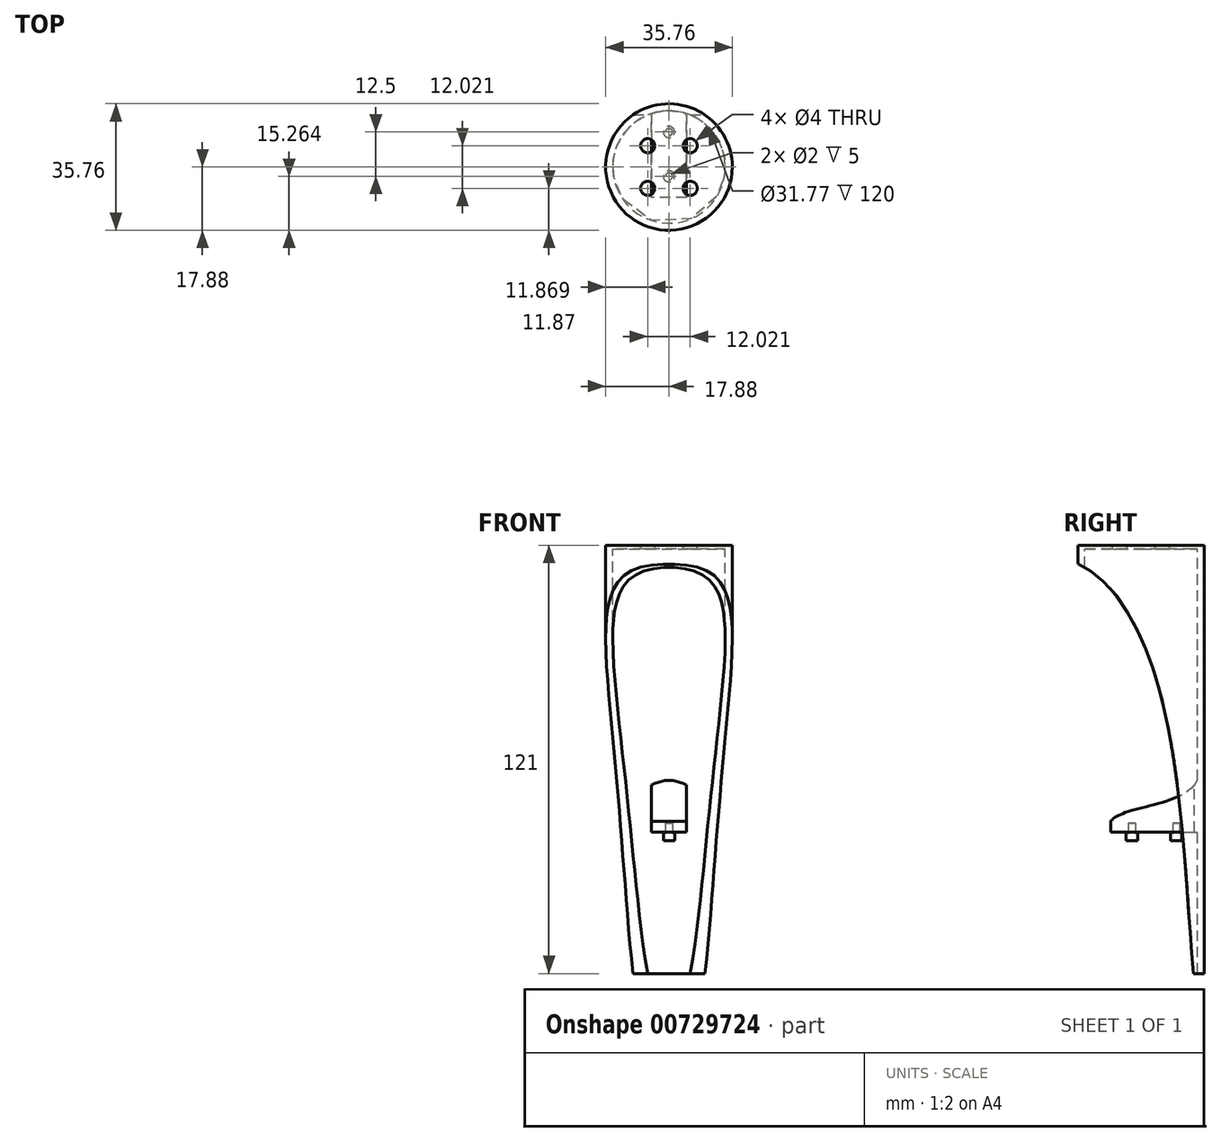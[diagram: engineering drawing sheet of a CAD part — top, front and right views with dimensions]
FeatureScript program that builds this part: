
annotation { "Feature Type Name" : "Feature", "Feature Type Description" : "" }
export const myFeature = defineFeature(function(context is Context, id is Id, definition is map)
    precondition{}
    {
        {
            var Q0;
            Q0=qCreatedBy(makeId("Top.planeOp"),FACE);
            var sketch = newSketch(context, id + "F0", { "sketchPlane" : qUnion([Q0])});
            skCircle(sketch, "E0", {"center": v(0, 0) * mm, "radius": 17.88 * mm});
            skSolve(sketch);
        }
        {
            var Q0;
            Q0=makeQuery(id+"F0.imprint","IMPRINT",FACE,{"disambiguationData":[TD([[makeQuery(id+"F0.imprint","IMPRINT",EDGE,{"derivedFrom":sQuery(id+"F0.wireOp",EDGE,"E0")}),1.0]])]});
            extrude(context, id + "F1", {"entities" : qUnion([Q0]), "depth" : 1 * mm, "offsetDistance" : 25 * mm});
        }
        {
            var Q0;
            Q0=makeQuery(id+"F1.opExtrude","CAP_FACE",FACE,{"disambiguationData":[OSD([sQuery(id+"F0.wireOp",EDGE,"E0")])],"isStart":true});
            var sketch = newSketch(context, id + "F2", { "sketchPlane" : qUnion([Q0])});
            skCircle(sketch, "E1", {"center": v(0, 0) * mm, "radius": 17.88 * mm});
            skCircle(sketch, "E2", {"center": v(0, 0) * mm, "radius": 15.88 * mm});
            skSolve(sketch);
        }
        {
            var Q0;
            Q0=qSketchRegion(id+"F2",true);
            extrude(context, id + "F3", {"entities" : qUnion([Q0]), "operationType" : NewBodyOperationType.ADD, "depth" : 120 * mm, "offsetDistance" : 25 * mm});
        }
        {
            var Q0;
            Q0=qCreatedBy(makeId("Right.planeOp"),FACE);
            var sketch = newSketch(context, id + "F4", { "sketchPlane" : qUnion([Q0])});
            skFitSpline(sketch, "E3", {"points": [v(-23.55, -2.93) * mm, v(2.93, -32.7) * mm, v(15.18, -125.34) * mm], "startDerivative": vector(85.56, -4.52) * mm, "endDerivative": vector(13.72, -154.47) * mm});
            skLineSegment(sketch, "E4", {"start": v(-23.55, -2.93) * mm, "end": v(-23.55, -130.52) * mm});
            skLineSegment(sketch, "E5", {"start": v(-23.55, -130.52) * mm, "end": v(15.18, -125.34) * mm});
            skSolve(sketch);
        }
        {
            var Q0;
            Q0=makeQuery(id+"F4.imprint","IMPRINT",FACE,{"disambiguationData":[TD([[makeQuery(id+"F4.imprint","IMPRINT",EDGE,{"derivedFrom":sQuery(id+"F4.wireOp",EDGE,"E3")}),-1.0]])]});
            extrude(context, id + "F5", {"entities" : qUnion([Q0]), "operationType" : NewBodyOperationType.REMOVE, "endBound" : BoundingType.SYMMETRIC, "oppositeDirection" : true, "depth" : 200 * mm, "offsetDistance" : 25 * mm});
        }
        {
            var Q0;
            Q0=makeQuery(id+"F1.opExtrude","CAP_FACE",FACE,{"disambiguationData":[OSD([sQuery(id+"F0.wireOp",EDGE,"E0")])],"isStart":false});
            var sketch = newSketch(context, id + "F6", { "sketchPlane" : qUnion([Q0])});
            skCircle(sketch, "E6", {"center": v(0, 0) * mm, "radius": 8.5 * mm, "construction": true});
            skCircle(sketch, "E7", {"center": v(-6.01, 6.01) * mm, "radius": 2 * mm});
            skCircle(sketch, "E8", {"center": v(6.01, 6.01) * mm, "radius": 2 * mm});
            skCircle(sketch, "E9", {"center": v(6.01, -6.01) * mm, "radius": 2 * mm});
            skCircle(sketch, "E10", {"center": v(-6.01, -6.01) * mm, "radius": 2 * mm});
            skSolve(sketch);
        }
        {
            var Q0;
            Q0=makeQuery(id+"F6.imprint","IMPRINT",FACE,{"disambiguationData":[TD([[makeQuery(id+"F6.imprint","IMPRINT",EDGE,{"derivedFrom":sQuery(id+"F6.wireOp",EDGE,"E7")}),1.0]])]});
            var Q1;
            Q1=makeQuery(id+"F6.imprint","IMPRINT",FACE,{"disambiguationData":[TD([[makeQuery(id+"F6.imprint","IMPRINT",EDGE,{"derivedFrom":sQuery(id+"F6.wireOp",EDGE,"E8")}),1.0]])]});
            var Q2;
            Q2=makeQuery(id+"F6.imprint","IMPRINT",FACE,{"disambiguationData":[TD([[makeQuery(id+"F6.imprint","IMPRINT",EDGE,{"derivedFrom":sQuery(id+"F6.wireOp",EDGE,"E9")}),1.0]])]});
            var Q3;
            Q3=makeQuery(id+"F6.imprint","IMPRINT",FACE,{"disambiguationData":[TD([[makeQuery(id+"F6.imprint","IMPRINT",EDGE,{"derivedFrom":sQuery(id+"F6.wireOp",EDGE,"E10")}),1.0]])]});
            extrude(context, id + "F7", {"entities" : qUnion([Q0, Q1, Q2, Q3]), "operationType" : NewBodyOperationType.REMOVE, "endBound" : BoundingType.THROUGH_ALL, "oppositeDirection" : true, "depth" : 25 * mm, "offsetDistance" : 25 * mm});
        }
        {
            var Q0;
            Q0=qCreatedBy(makeId("Right.planeOp"),FACE);
            var sketch = newSketch(context, id + "F8", { "sketchPlane" : qUnion([Q0])});
            skFitSpline(sketch, "E11", {"points": [v(16.38, -63) * mm, v(-1.68, -73.65) * mm, v(-8.62, -77) * mm], "startDerivative": vector(0, -33.73) * mm, "endDerivative": vector(-5.99, -9.37) * mm});
            skLineSegment(sketch, "E12.bottom", {"start": v(-8.62, -77) * mm, "end": v(16.38, -77) * mm});
            skLineSegment(sketch, "E12.top", {"start": v(-8.62, -80) * mm, "end": v(16.38, -80) * mm});
            skLineSegment(sketch, "E12.left", {"start": v(-8.62, -77) * mm, "end": v(-8.62, -80) * mm});
            skLineSegment(sketch, "E12.right", {"start": v(16.38, -77) * mm, "end": v(16.38, -80) * mm});
            skLineSegment(sketch, "E13", {"start": v(16.38, -63) * mm, "end": v(16.38, -77) * mm});
            skLineSegment(sketch, "E14", {"start": v(-17.88, -4.26) * mm, "end": v(-17.88, 1) * mm});
            skLineSegment(sketch, "E15", {"start": v(17.88, 1) * mm, "end": v(17.88, -120) * mm});
            skSolve(sketch);
        }
        {
            var Q0;
            {var subQ0=sQuery(id+"F8.wireOp",EDGE,"E11");Q0=makeQuery(id+"F8.imprint","IMPRINT",FACE,{"disambiguationData":[TD([[makeQuery(id+"F8.imprint","IMPRINT",EDGE,{"derivedFrom":subQ0}),1.0]])]});}
            var Q1;
            {var subQ0=sQuery(id+"F8.wireOp",EDGE,"E12.bottom");Q1=makeQuery(id+"F8.imprint","IMPRINT",FACE,{"disambiguationData":[TD([[makeQuery(id+"F8.imprint","IMPRINT",EDGE,{"derivedFrom":subQ0}),-1.0]])]});}
            extrude(context, id + "F9", {"entities" : qUnion([Q0, Q1]), "operationType" : NewBodyOperationType.ADD, "endBound" : BoundingType.SYMMETRIC, "depth" : 10 * mm, "offsetDistance" : 25 * mm});
        }
        {
            var Q0;
            Q0=makeQuery(id+"F9.opExtrude","SWEPT_FACE",FACE,{"disambiguationData":[OSD([sQuery(id+"F8.wireOp",EDGE,"E12.top")])]});
            var sketch = newSketch(context, id + "F10", { "sketchPlane" : qUnion([Q0])});
            skCircle(sketch, "E16", {"center": v(0, -9.88) * mm, "radius": 1.6 * mm});
            skCircle(sketch, "E17", {"center": v(0, 2.62) * mm, "radius": 1.6 * mm});
            skSolve(sketch);
        }
        {
            var Q0;
            {var subQ0=sQuery(id+"F10.wireOp",EDGE,"E17");var subQ1=makeQuery(id+"F9.opExtrude","SWEPT_EDGE",EDGE,{"disambiguationData":[OSD([sQuery(id+"F8.wireOp",EDGE,"E12.top"),sQuery(id+"F8.wireOp",EDGE,"E12.left")])]});var subQ2=makeQuery(id+"F10.imprint","INTERSECT",VERTEX,{"disambiguationData":[OD(0.0)],"derivedFrom":[subQ1,subQ0]});Q0=makeQuery(id+"F10.imprint","IMPRINT",FACE,{"disambiguationData":[TD([[makeQuery(id+"F10.imprint","IMPRINT",EDGE,{"disambiguationData":[TD([[subQ2,-1.0]])],"derivedFrom":subQ0}),1.0]])]});}
            var Q1;
            {var subQ0=sQuery(id+"F10.wireOp",EDGE,"E17");var subQ1=makeQuery(id+"F9.opExtrude","SWEPT_EDGE",EDGE,{"disambiguationData":[OSD([sQuery(id+"F8.wireOp",EDGE,"E12.top"),sQuery(id+"F8.wireOp",EDGE,"E12.left")])]});var subQ2=makeQuery(id+"F10.imprint","INTERSECT",VERTEX,{"disambiguationData":[OD(0.0)],"derivedFrom":[subQ1,subQ0]});Q1=makeQuery(id+"F10.imprint","IMPRINT",FACE,{"disambiguationData":[TD([[makeQuery(id+"F10.imprint","IMPRINT",EDGE,{"disambiguationData":[TD([[subQ2,1.0]])],"derivedFrom":subQ0}),1.0]])]});}
            var Q2;
            Q2=makeQuery(id+"F10.imprint","IMPRINT",FACE,{"disambiguationData":[TD([[makeQuery(id+"F10.imprint","IMPRINT",EDGE,{"derivedFrom":sQuery(id+"F10.wireOp",EDGE,"E16")}),1.0]])]});
            extrude(context, id + "F11", {"entities" : qUnion([Q0, Q1, Q2]), "operationType" : NewBodyOperationType.ADD, "depth" : 2.5 * mm, "offsetDistance" : 25 * mm});
        }
        {
            var Q0;
            Q0=makeQuery(id+"F11.opExtrude","CAP_FACE",FACE,{"disambiguationData":[OSD([sQuery(id+"F10.wireOp",EDGE,"E17")])],"isStart":false});
            var sketch = newSketch(context, id + "F12", { "sketchPlane" : qUnion([Q0])});
            skCircle(sketch, "E18", {"center": v(0, 2.62) * mm, "radius": 1 * mm});
            skCircle(sketch, "E19", {"center": v(0, -9.88) * mm, "radius": 1 * mm});
            skSolve(sketch);
        }
        {
            var Q0;
            Q0=makeQuery(id+"F12.imprint","IMPRINT",FACE,{"disambiguationData":[TD([[makeQuery(id+"F12.imprint","IMPRINT",EDGE,{"derivedFrom":sQuery(id+"F12.wireOp",EDGE,"E18")}),1.0]])]});
            var Q1;
            Q1=makeQuery(id+"F12.imprint","IMPRINT",FACE,{"disambiguationData":[TD([[makeQuery(id+"F12.imprint","IMPRINT",EDGE,{"derivedFrom":sQuery(id+"F12.wireOp",EDGE,"E19")}),1.0]])]});
            extrude(context, id + "F13", {"entities" : qUnion([Q0, Q1]), "operationType" : NewBodyOperationType.REMOVE, "oppositeDirection" : true, "depth" : 5 * mm, "offsetDistance" : 25 * mm});
        }
    });
